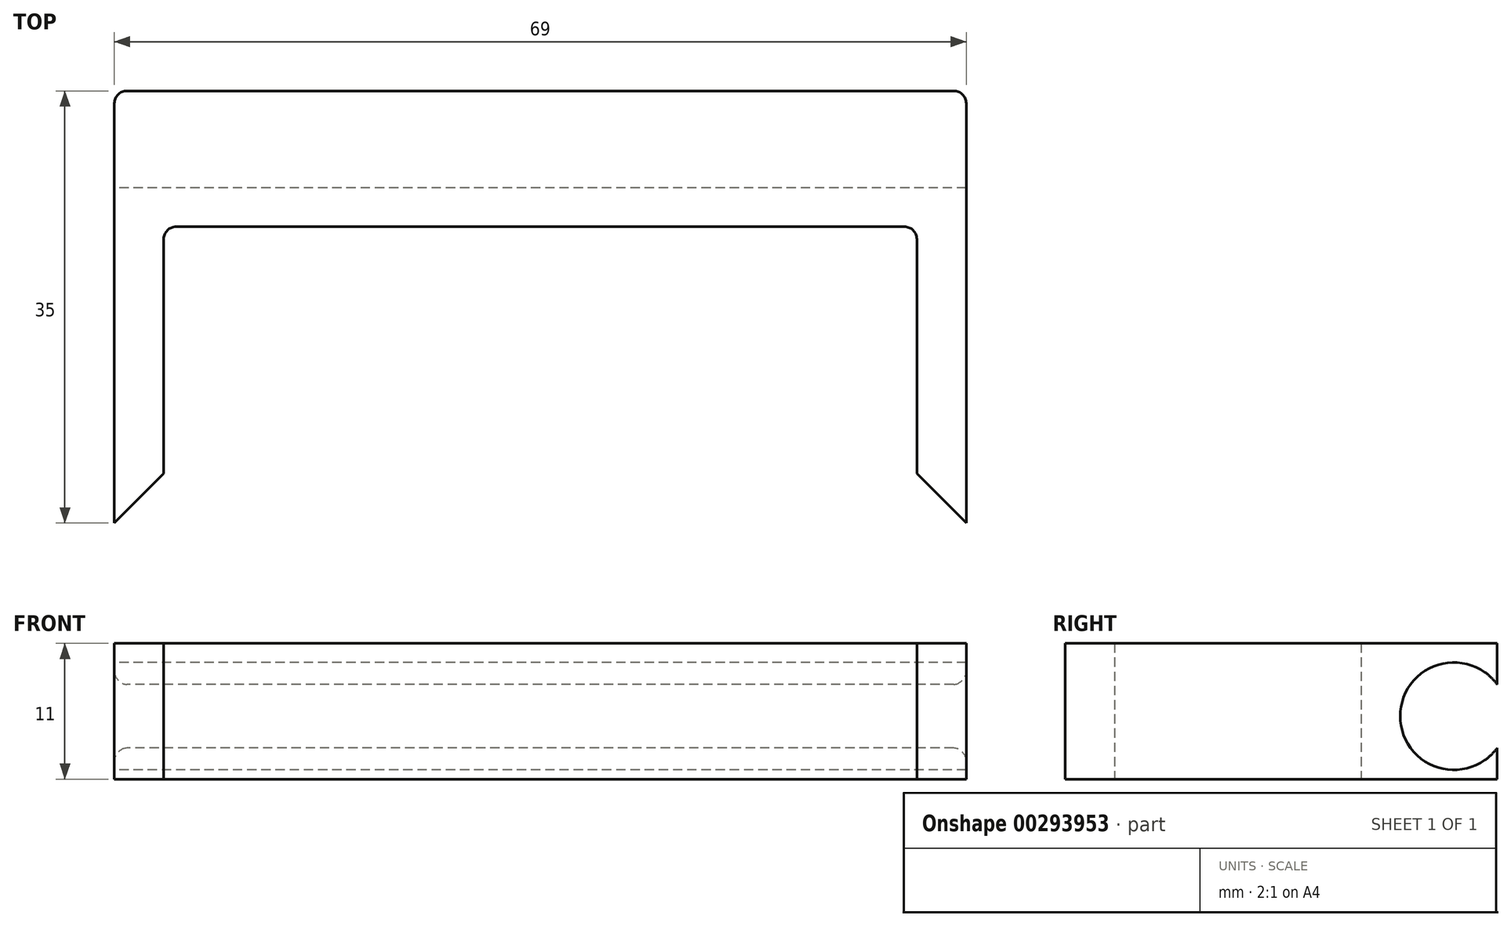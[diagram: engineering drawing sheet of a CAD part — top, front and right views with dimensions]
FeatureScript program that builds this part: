
annotation { "Feature Type Name" : "Feature", "Feature Type Description" : "" }
export const myFeature = defineFeature(function(context is Context, id is Id, definition is map)
    precondition{}
    {
        {
            var Q0;
            Q0=qCreatedBy(makeId("Top.planeOp"),FACE);
            var sketch = newSketch(context, id + "F0", { "sketchPlane" : qUnion([Q0])});
            skLineSegment(sketch, "E0", {"start": v(-61, -25) * mm, "end": v(-61, 0) * mm});
            skLineSegment(sketch, "E1", {"start": v(0, 0) * mm, "end": v(-61, 0) * mm});
            skLineSegment(sketch, "E2", {"start": v(0, 0) * mm, "end": v(0, -25) * mm});
            skLineSegment(sketch, "E3", {"start": v(0, -25) * mm, "end": v(4, -25) * mm});
            skLineSegment(sketch, "E4", {"start": v(4, -25) * mm, "end": v(4, 11) * mm});
            skLineSegment(sketch, "E5", {"start": v(4, 11) * mm, "end": v(-65, 11) * mm});
            skLineSegment(sketch, "E6", {"start": v(-65, 11) * mm, "end": v(-65, -25) * mm});
            skLineSegment(sketch, "E7", {"start": v(-65, -25) * mm, "end": v(-61, -25) * mm});
            skSolve(sketch);
        }
        {
            var Q0;
            Q0 = qSketchRegion(id + "F0", true);
            extrude(context, id + "F1", {"entities" : qUnion([Q0]), "depth" : 11 * mm, "offsetDistance" : 25 * mm});
        }
        {
            var Q0;
            Q0=makeQuery(id+"F1.opExtrude","SWEPT_EDGE",EDGE,{"disambiguationData":[OSD([sQuery(id+"F0.wireOp",EDGE,"E2"),sQuery(id+"F0.wireOp",EDGE,"E3")])]});
            chamfer(context, id + "F2", {"entities" : qUnion([Q0]), "width" : 5 * mm, "tangentPropagation" : true});
        }
        {
            var Q0;
            Q0=makeQuery(id+"F1.opExtrude","SWEPT_FACE",FACE,{"disambiguationData":[OSD([sQuery(id+"F0.wireOp",EDGE,"E6")])]});
            var sketch = newSketch(context, id + "F3", { "sketchPlane" : qUnion([Q0])});
            skCircle(sketch, "E8", {"center": v(-7.5, 5.1) * mm, "radius": 4.35 * mm});
            skSolve(sketch);
        }
        {
            var Q0;
            Q0 = qSketchRegion(id + "F3", true);
            extrude(context, id + "F4", {"entities" : qUnion([Q0]), "operationType" : NewBodyOperationType.REMOVE, "endBound" : BoundingType.THROUGH_ALL, "oppositeDirection" : true, "depth" : 25 * mm, "offsetDistance" : 25 * mm});
        }
        {
            var Q0;
            Q0=makeQuery(id+"F1.opExtrude","SWEPT_EDGE",EDGE,{"disambiguationData":[OSD([sQuery(id+"F0.wireOp",EDGE,"E0"),sQuery(id+"F0.wireOp",EDGE,"E7")])]});
            chamfer(context, id + "F5", {"entities" : qUnion([Q0]), "width" : 5 * mm, "tangentPropagation" : true});
        }
        {
            var Q0;
            Q0=makeQuery(id+"F1.opExtrude","SWEPT_EDGE",EDGE,{"disambiguationData":[OSD([sQuery(id+"F0.wireOp",EDGE,"E0"),sQuery(id+"F0.wireOp",EDGE,"E1")])]});
            var Q1;
            Q1=makeQuery(id+"F1.opExtrude","SWEPT_EDGE",EDGE,{"disambiguationData":[OSD([sQuery(id+"F0.wireOp",EDGE,"E1"),sQuery(id+"F0.wireOp",EDGE,"E2")])]});
            var Q2;
            Q2=makeQuery(id+"F1.opExtrude","SWEPT_EDGE",EDGE,{"disambiguationData":[OSD([sQuery(id+"F0.wireOp",EDGE,"E4"),sQuery(id+"F0.wireOp",EDGE,"E5")])]});
            var Q3;
            {var subQ0=sQuery(id+"F0.wireOp",EDGE,"E6");var subQ1=sQuery(id+"F0.wireOp",EDGE,"E5");Q3=makeQuery(id+"F4.boolean.opBoolean","SPLIT",EDGE,{"disambiguationData":[TD([makeQuery(id+"F1.opExtrude","CAP_FACE",FACE,{"disambiguationData":[OSD([sQuery(id+"F0.wireOp",EDGE,"E0"),sQuery(id+"F0.wireOp",EDGE,"E1"),sQuery(id+"F0.wireOp",EDGE,"E2"),sQuery(id+"F0.wireOp",EDGE,"E3"),sQuery(id+"F0.wireOp",EDGE,"E4"),subQ1,subQ0,sQuery(id+"F0.wireOp",EDGE,"E7")])],"isStart":false})])],"derivedFrom":makeQuery(id+"F1.opExtrude","SWEPT_EDGE",EDGE,{"disambiguationData":[OSD([subQ1,subQ0])]})});}
            var Q4;
            {var subQ0=sQuery(id+"F0.wireOp",EDGE,"E6");var subQ1=sQuery(id+"F0.wireOp",EDGE,"E5");Q4=makeQuery(id+"F4.boolean.opBoolean","SPLIT",EDGE,{"disambiguationData":[TD([makeQuery(id+"F1.opExtrude","CAP_FACE",FACE,{"disambiguationData":[OSD([sQuery(id+"F0.wireOp",EDGE,"E0"),sQuery(id+"F0.wireOp",EDGE,"E1"),sQuery(id+"F0.wireOp",EDGE,"E2"),sQuery(id+"F0.wireOp",EDGE,"E3"),sQuery(id+"F0.wireOp",EDGE,"E4"),subQ1,subQ0,sQuery(id+"F0.wireOp",EDGE,"E7")])],"isStart":true})])],"derivedFrom":makeQuery(id+"F1.opExtrude","SWEPT_EDGE",EDGE,{"disambiguationData":[OSD([subQ1,subQ0])]})});}
            var Q5;
            {var subQ0=sQuery(id+"F0.wireOp",EDGE,"E7");var subQ1=sQuery(id+"F0.wireOp",EDGE,"E6");Q5=makeQuery(id+"F4.boolean.opBoolean","SPLIT",EDGE,{"disambiguationData":[TD([makeQuery(id+"F1.opExtrude","CAP_FACE",FACE,{"disambiguationData":[OSD([sQuery(id+"F0.wireOp",EDGE,"E0"),sQuery(id+"F0.wireOp",EDGE,"E1"),sQuery(id+"F0.wireOp",EDGE,"E2"),sQuery(id+"F0.wireOp",EDGE,"E3"),sQuery(id+"F0.wireOp",EDGE,"E4"),sQuery(id+"F0.wireOp",EDGE,"E5"),subQ1,subQ0])],"isStart":false})])],"derivedFrom":makeQuery(id+"F1.opExtrude","SWEPT_EDGE",EDGE,{"disambiguationData":[OSD([subQ1,subQ0])]})});}
            var Q6;
            {var subQ0=sQuery(id+"F0.wireOp",EDGE,"E7");var subQ1=sQuery(id+"F0.wireOp",EDGE,"E6");Q6=makeQuery(id+"F4.boolean.opBoolean","SPLIT",EDGE,{"disambiguationData":[TD([makeQuery(id+"F1.opExtrude","CAP_FACE",FACE,{"disambiguationData":[OSD([sQuery(id+"F0.wireOp",EDGE,"E0"),sQuery(id+"F0.wireOp",EDGE,"E1"),sQuery(id+"F0.wireOp",EDGE,"E2"),sQuery(id+"F0.wireOp",EDGE,"E3"),sQuery(id+"F0.wireOp",EDGE,"E4"),sQuery(id+"F0.wireOp",EDGE,"E5"),subQ1,subQ0])],"isStart":true})])],"derivedFrom":makeQuery(id+"F1.opExtrude","SWEPT_EDGE",EDGE,{"disambiguationData":[OSD([subQ1,subQ0])]})});}
            fillet(context, id + "F6", {"entities" : qUnion([Q0, Q1, Q2, Q3, Q4, Q5, Q6]), "radius" : 1 * mm, "tangentPropagation" : true, "allowEdgeOverflow" : false});
        }
    });
